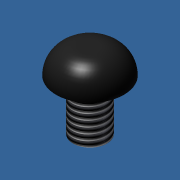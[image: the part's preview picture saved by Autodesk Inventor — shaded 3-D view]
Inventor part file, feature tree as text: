
AUTODESK INVENTOR PART (.ipt)
format: ipt  version: 2012 (Build 160160000, 160)  size: 105,984 bytes
history: native  units: mm
features: extrude x2, sketch x2, other x1, fillet x1, thread x1
ambient origin geometry x1: Origin
feature tree (7):
  other  "ソリッド1"
  extrude  "押し出し1"  Depth=4.0mm
  extrude  "押し出し2"  Depth=6.0mm TaperAngle=0.0deg
  fillet  "フィレット1"  Radius=8.0mm
  thread  "ねじ1"
  sketch  "スケッチ1"
  sketch  "スケッチ2"
